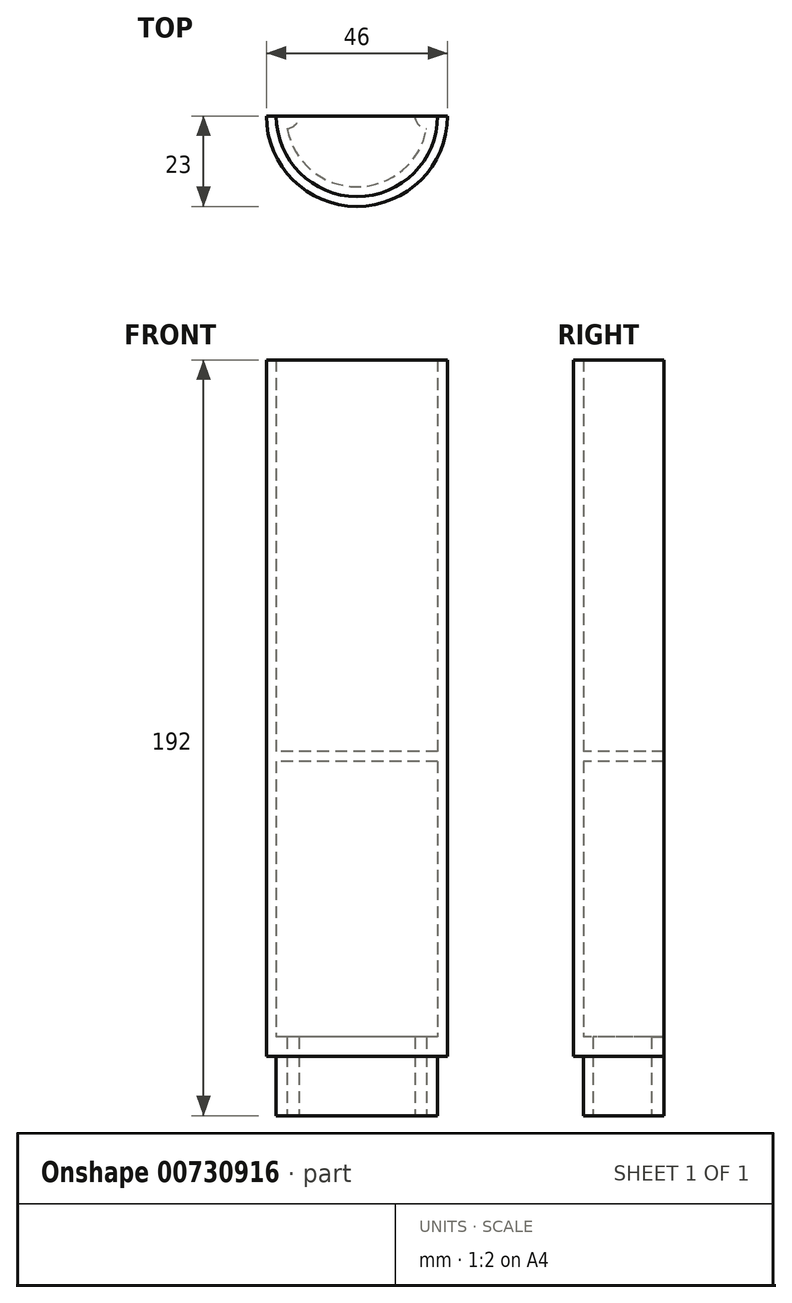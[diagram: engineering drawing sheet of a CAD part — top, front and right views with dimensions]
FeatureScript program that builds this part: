
annotation { "Feature Type Name" : "Feature", "Feature Type Description" : "" }
export const myFeature = defineFeature(function(context is Context, id is Id, definition is map)
    precondition{}
    {
        {
            var Q0;
            Q0=qCreatedBy(makeId("Front.planeOp"),FACE);
            var sketch = newSketch(context, id + "F0", { "sketchPlane" : qUnion([Q0])});
            skLineSegment(sketch, "E0.top", {"start": v(0, 2.5) * mm, "end": v(20.5, 2.5) * mm});
            skLineSegment(sketch, "E0.right", {"start": v(20.5, 102) * mm, "end": v(20.5, 2.5) * mm});
            skLineSegment(sketch, "E1", {"start": v(20.5, 102) * mm, "end": v(23, 102) * mm});
            skLineSegment(sketch, "E2", {"start": v(23, 102) * mm, "end": v(23, 0) * mm});
            skLineSegment(sketch, "E3", {"start": v(0, 0) * mm, "end": v(0, 2.5) * mm});
            skLineSegment(sketch, "E4", {"start": v(23, 0) * mm, "end": v(23, -75) * mm});
            skLineSegment(sketch, "E5", {"start": v(23, -75) * mm, "end": v(20.5, -75) * mm});
            skLineSegment(sketch, "E6", {"start": v(0, 0) * mm, "end": v(20.5, 0) * mm});
            skLineSegment(sketch, "E7", {"start": v(20.5, -75) * mm, "end": v(20.5, -90) * mm});
            skLineSegment(sketch, "E8", {"start": v(20.5, -90) * mm, "end": v(18, -90) * mm});
            skLineSegment(sketch, "E9", {"start": v(18, -90) * mm, "end": v(18, -70) * mm});
            skLineSegment(sketch, "E10", {"start": v(18, -70) * mm, "end": v(20.5, -70) * mm});
            skLineSegment(sketch, "E11", {"start": v(20.5, 0) * mm, "end": v(20.5, -70) * mm});
            skSolve(sketch);
        }
        {
            var Q0;
            Q0=qSketchRegion(id+"F0",true);
            var Q1;
            Q1=sQuery(id+"F0.wireOp",EDGE,"E3");
            revolve(context, id + "F1", {"surfaceOperationType" : NewSurfaceOperationType.NEW, "entities" : qUnion([Q0]), "axis" : qUnion([Q1]), "revolveType" : RevolveType.FULL});
        }
        {
            var Q0;
            Q0=makeQuery(id+"F1.opRevolve","SWEPT_FACE",FACE,{"disambiguationData":[OSD([sQuery(id+"F0.wireOp",EDGE,"E0.top")])]});
            var sketch = newSketch(context, id + "F2", { "sketchPlane" : qUnion([Q0])});
            skCircle(sketch, "E12", {"center": v(0, 0) * mm, "radius": 20.5 * mm});
            skLineSegment(sketch, "E13", {"start": v(0, 20.5) * mm, "end": v(0, 12.5) * mm});
            skLineSegment(sketch, "E14", {"start": v(0, 12.5) * mm, "end": v(16.25, 12.5) * mm});
            skSolve(sketch);
        }
        {
            var Q0;
            {var subQ0=sQuery(id+"F2.wireOp",EDGE,"E13");Q0=makeQuery(id+"F2.imprint","IMPRINT",FACE,{"disambiguationData":[TD([[makeQuery(id+"F2.imprint","IMPRINT",EDGE,{"derivedFrom":subQ0}),1.0]])]});}
            var Q1;
            Q1=makeQuery(id+"F1.opRevolve","SWEPT_FACE",FACE,{"disambiguationData":[OSD([sQuery(id+"F0.wireOp",EDGE,"E6")])]});
            extrude(context, id + "F3", {"entities" : qUnion([Q0]), "operationType" : NewBodyOperationType.REMOVE, "endBound" : BoundingType.UP_TO_SURFACE, "oppositeDirection" : true, "depth" : 25 * mm, "endBoundEntityFace" : qUnion([Q1]), "offsetDistance" : 25 * mm});
        }
        {
            var Q0;
            Q0=makeQuery(id+"F1.opRevolve","SWEPT_FACE",FACE,{"disambiguationData":[OSD([sQuery(id+"F0.wireOp",EDGE,"E8")])]});
            var sketch = newSketch(context, id + "F4", { "sketchPlane" : qUnion([Q0])});
            skArc(sketch, "E15", {"start": v(-17.7, -3.24) * mm, "mid": v(-14.75, 0) * mm, "end": v(-17.7, 3.24) * mm});
            skArc(sketch, "E16", {"start": v(17.7, 3.24) * mm, "mid": v(14.75, 0) * mm, "end": v(17.7, -3.24) * mm});
            skArc(sketch, "E17", {"start": v(17.7, -3.24) * mm, "mid": v(18, 0) * mm, "end": v(17.7, 3.24) * mm});
            skArc(sketch, "E18", {"start": v(-17.7, -3.24) * mm, "mid": v(-18, 0) * mm, "end": v(-17.7, 3.24) * mm});
            skSolve(sketch);
        }
        {
            var Q0;
            Q0=qSketchRegion(id+"F4",true);
            var Q1;
            Q1=makeQuery(id+"F1.opRevolve","SWEPT_FACE",FACE,{"disambiguationData":[OSD([sQuery(id+"F0.wireOp",EDGE,"E10")])]});
            extrude(context, id + "F5", {"entities" : qUnion([Q0]), "operationType" : NewBodyOperationType.ADD, "endBound" : BoundingType.UP_TO_SURFACE, "oppositeDirection" : true, "depth" : 25 * mm, "endBoundEntityFace" : qUnion([Q1]), "offsetDistance" : 25 * mm});
        }
        {
            var Q0;
            Q0=makeQuery(id+"F1.opRevolve","SWEPT_FACE",FACE,{"disambiguationData":[OSD([sQuery(id+"F0.wireOp",EDGE,"E1")])]});
            var sketch = newSketch(context, id + "F6", { "sketchPlane" : qUnion([Q0])});
            skArc(sketch, "E19", {"start": v(23, 0) * mm, "mid": v(0, 23) * mm, "end": v(-23, 0) * mm});
            skLineSegment(sketch, "E20", {"start": v(-23, 0) * mm, "end": v(23, 0) * mm});
            skSolve(sketch);
        }
        {
            var Q0;
            Q0 = qSketchRegion(id + "F6", true);
            extrude(context, id + "F7", {"entities" : qUnion([Q0]), "operationType" : NewBodyOperationType.REMOVE, "endBound" : BoundingType.THROUGH_ALL, "oppositeDirection" : true, "depth" : 25 * mm, "offsetDistance" : 25 * mm});
        }
    });
